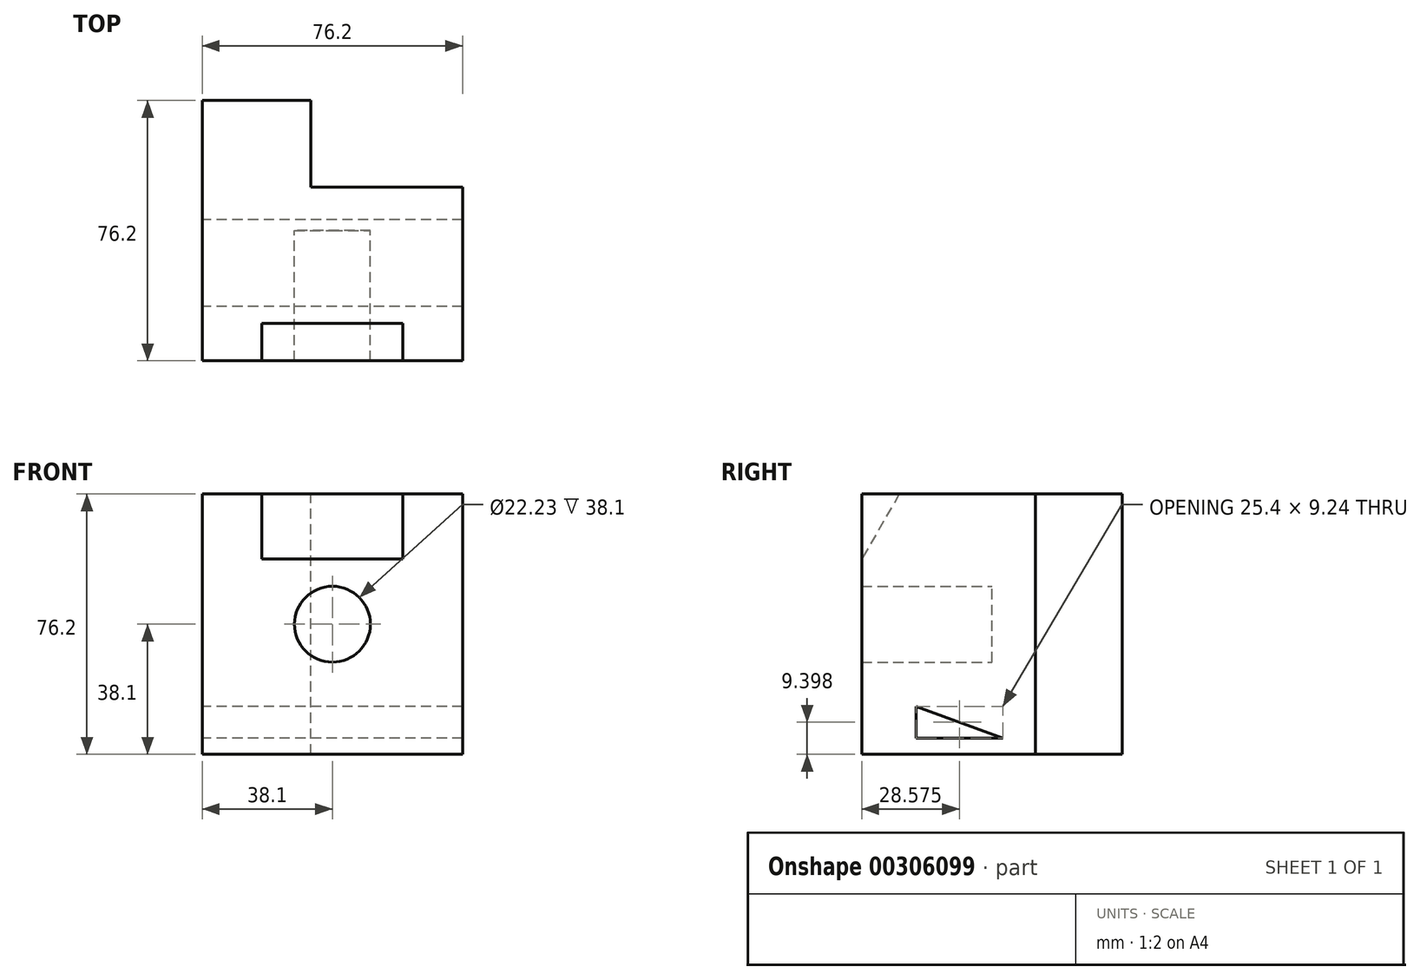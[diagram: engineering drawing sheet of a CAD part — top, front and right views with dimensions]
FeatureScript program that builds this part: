
annotation { "Feature Type Name" : "Feature", "Feature Type Description" : "" }
export const myFeature = defineFeature(function(context is Context, id is Id, definition is map)
    precondition{}
    {
        {
            var Q0;
            Q0=qCreatedBy(makeId("Front.planeOp"),FACE);
            var sketch = newSketch(context, id + "F0", { "sketchPlane" : qUnion([Q0])});
            skLineSegment(sketch, "E0.bottom", {"start": v(38.1, 38.1) * mm, "end": v(-38.1, 38.1) * mm});
            skLineSegment(sketch, "E0.top", {"start": v(38.1, -38.1) * mm, "end": v(-38.1, -38.1) * mm});
            skLineSegment(sketch, "E0.left", {"start": v(38.1, 38.1) * mm, "end": v(38.1, -38.1) * mm});
            skLineSegment(sketch, "E0.right", {"start": v(-38.1, 38.1) * mm, "end": v(-38.1, -38.1) * mm});
            skPoint(sketch, "E0.middle", {"position": v(0, 0) * mm});
            skCircle(sketch, "E1", {"center": v(0, 0) * mm, "radius": 11.11 * mm, "construction": true});
            skSolve(sketch);
        }
        {
            var Q0;
            Q0 = qSketchRegion(id + "F0", true);
            extrude(context, id + "F1", {"entities" : qUnion([Q0]), "endBound" : BoundingType.SYMMETRIC, "depth" : 76.2 * mm});
        }
        {
            var Q0;
            Q0=qCreatedBy(makeId("Front.planeOp"),FACE);
            var sketch = newSketch(context, id + "F2", { "sketchPlane" : qUnion([Q0])});
            skCircle(sketch, "E2.0", {"center": v(0, 0) * mm, "radius": 11.11 * mm});
            skSolve(sketch);
        }
        {
            var Q0;
            Q0 = qSketchRegion(id + "F2", true);
            var Q1;
            Q1=makeQuery(id+"F1.opExtrude","CAP_FACE",FACE,{"disambiguationData":[OSD([sQuery(id+"F0.wireOp",EDGE,"E0.bottom"),sQuery(id+"F0.wireOp",EDGE,"E0.top"),sQuery(id+"F0.wireOp",EDGE,"E0.left"),sQuery(id+"F0.wireOp",EDGE,"E0.right")])],"isStart":false});
            extrude(context, id + "F3", {"entities" : qUnion([Q0]), "operationType" : NewBodyOperationType.REMOVE, "endBound" : BoundingType.THROUGH_ALL, "endBoundEntityFace" : qUnion([Q1]), "depth" : 25.4 * mm});
        }
        {
            var Q0;
            Q0=makeQuery(id+"F1.opExtrude","SWEPT_FACE",FACE,{"disambiguationData":[OSD([sQuery(id+"F0.wireOp",EDGE,"E0.bottom")])]});
            var sketch = newSketch(context, id + "F4", { "sketchPlane" : qUnion([Q0])});
            skLineSegment(sketch, "E3.bottom", {"start": v(38.1, 38.1) * mm, "end": v(-6.35, 38.1) * mm});
            skLineSegment(sketch, "E3.top", {"start": v(38.1, 12.7) * mm, "end": v(-6.35, 12.7) * mm});
            skLineSegment(sketch, "E3.left", {"start": v(38.1, 38.1) * mm, "end": v(38.1, 12.7) * mm});
            skLineSegment(sketch, "E3.right", {"start": v(-6.35, 38.1) * mm, "end": v(-6.35, 12.7) * mm});
            skSolve(sketch);
        }
        {
            var Q0;
            Q0=qCreatedBy(makeId("Right.planeOp"),FACE);
            var sketch = newSketch(context, id + "F5", { "sketchPlane" : qUnion([Q0])});
            skLineSegment(sketch, "E4", {"start": v(-27.1, 38.1) * mm, "end": v(-38.1, 19.05) * mm});
            skLineSegment(sketch, "E5.0", {"start": v(-38.1, 38.1) * mm, "end": v(-27.1, 38.1) * mm});
            skLineSegment(sketch, "E5.1", {"start": v(-38.1, 38.1) * mm, "end": v(-38.1, 19.05) * mm});
            skPoint(sketch, "E6.orphan", {"position": v(38.1, 38.1) * mm});
            skPoint(sketch, "E7.orphan", {"position": v(-38.1, -38.1) * mm});
            skSolve(sketch);
        }
        {
            var Q0;
            Q0 = qSketchRegion(id + "F5", true);
            extrude(context, id + "F6", {"entities" : qUnion([Q0]), "operationType" : NewBodyOperationType.REMOVE, "endBound" : BoundingType.SYMMETRIC, "oppositeDirection" : true, "depth" : 41.27 * mm});
        }
        {
            var Q0;
            Q0 = qSketchRegion(id + "F4", true);
            extrude(context, id + "F7", {"entities" : qUnion([Q0]), "operationType" : NewBodyOperationType.REMOVE, "endBound" : BoundingType.THROUGH_ALL, "oppositeDirection" : true, "depth" : 25.4 * mm});
        }
        {
            var Q0;
            Q0=makeQuery(id+"F1.opExtrude","SWEPT_FACE",FACE,{"disambiguationData":[OSD([sQuery(id+"F0.wireOp",EDGE,"E0.right")])]});
            var sketch = newSketch(context, id + "F8", { "sketchPlane" : qUnion([Q0])});
            skLineSegment(sketch, "E8", {"start": v(-3.17, -33.32) * mm, "end": v(22.23, -33.32) * mm});
            skLineSegment(sketch, "E9", {"start": v(22.22, -33.32) * mm, "end": v(22.22, -24.08) * mm});
            skLineSegment(sketch, "E10", {"start": v(22.23, -24.08) * mm, "end": v(-3.18, -33.32) * mm});
            skSolve(sketch);
        }
        {
            var Q0;
            Q0 = qSketchRegion(id + "F8", true);
            extrude(context, id + "F9", {"entities" : qUnion([Q0]), "operationType" : NewBodyOperationType.REMOVE, "endBound" : BoundingType.THROUGH_ALL, "oppositeDirection" : true, "depth" : 25.4 * mm});
        }
    });
